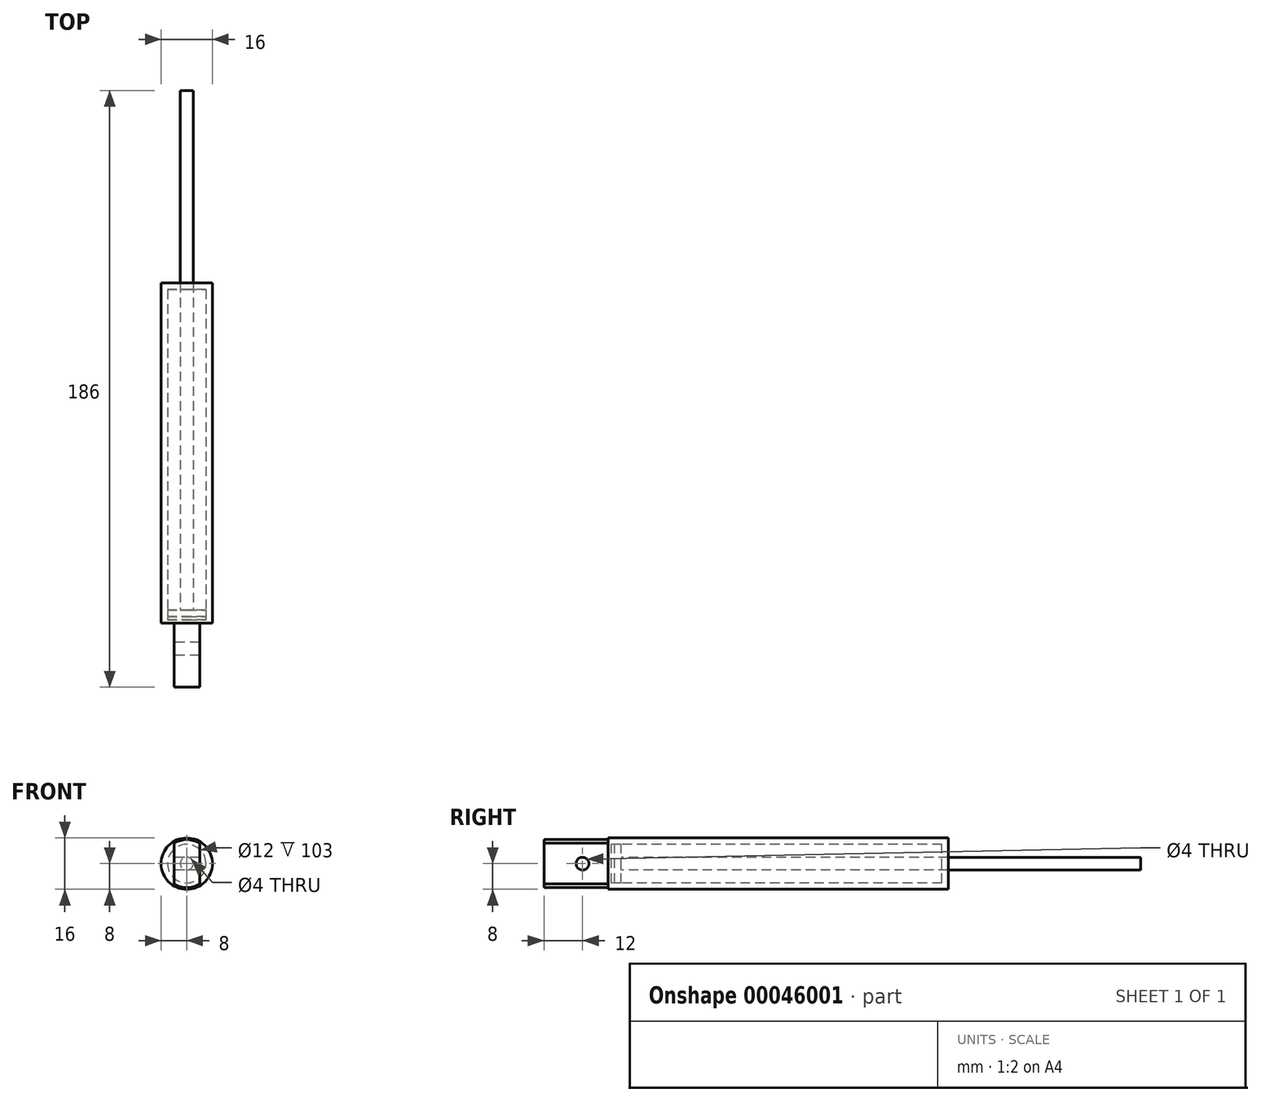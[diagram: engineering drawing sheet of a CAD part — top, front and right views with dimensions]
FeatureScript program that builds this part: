
annotation { "Feature Type Name" : "Feature", "Feature Type Description" : "" }
export const myFeature = defineFeature(function(context is Context, id is Id, definition is map)
    precondition{}
    {
        {
            var Q0;
            Q0=qCreatedBy(makeId("Right.planeOp"),FACE);
            var sketch = newSketch(context, id + "F0", { "sketchPlane" : qUnion([Q0])});
            skLineSegment(sketch, "E0", {"start": v(-96, 0) * mm, "end": v(96, 0) * mm});
            skLineSegment(sketch, "E1", {"start": v(-76, 7.5) * mm, "end": v(-76, 8) * mm});
            skLineSegment(sketch, "E2", {"start": v(-76, 8) * mm, "end": v(30, 8) * mm});
            skLineSegment(sketch, "E3", {"start": v(30, 8) * mm, "end": v(30, 2) * mm});
            skPoint(sketch, "E4.visualSharp", {"position": v(-76, 0) * mm});
            skLineSegment(sketch, "E5", {"start": v(-72, 2) * mm, "end": v(90, 2) * mm});
            skLineSegment(sketch, "E6", {"start": v(-76, 7.5) * mm, "end": v(-96, 7.5) * mm});
            skLineSegment(sketch, "E7", {"start": v(-96, 7.5) * mm, "end": v(-96, 0) * mm});
            skCircle(sketch, "E8", {"center": v(-84, 0) * mm, "radius": 2 * mm});
            skLineSegment(sketch, "E9", {"start": v(90, 2) * mm, "end": v(90, 0) * mm});
            skLineSegment(sketch, "E10", {"start": v(30, 2) * mm, "end": v(28, 2) * mm});
            skLineSegment(sketch, "E11", {"start": v(28, 2) * mm, "end": v(28, 6) * mm});
            skLineSegment(sketch, "E12", {"start": v(28, 6) * mm, "end": v(-75, 6) * mm});
            skLineSegment(sketch, "E13", {"start": v(-75, 6) * mm, "end": v(-75, 0) * mm});
            skLineSegment(sketch, "E14", {"start": v(-72, 2) * mm, "end": v(-72, 6) * mm});
            skLineSegment(sketch, "E15", {"start": v(-72, 6) * mm, "end": v(-74, 6) * mm});
            skLineSegment(sketch, "E16", {"start": v(-74, 6) * mm, "end": v(-74, 0) * mm});
            skSolve(sketch);
        }
        {
            var Q0;
            Q0=makeQuery(id+"F0.imprint","IMPRINT",FACE,{"disambiguationData":[TD([[makeQuery(id+"F0.imprint","IMPRINT",EDGE,{"derivedFrom":sQuery(id+"F0.wireOp",EDGE,"E1")}),-1.0]])]});
            var Q1;
            {var subQ0=sQuery(id+"F0.wireOp",EDGE,"E8");var subQ1=sQuery(id+"F0.wireOp",EDGE,"E0");var subQ3=makeQuery(id+"F0.imprint","INTERSECT",VERTEX,{"disambiguationData":[OD(0.0)],"derivedFrom":[subQ1,subQ0]});Q1=makeQuery(id+"F0.imprint","IMPRINT",FACE,{"disambiguationData":[TD([[makeQuery(id+"F0.imprint","IMPRINT",EDGE,{"disambiguationData":[TD([[subQ3,-1.0]])],"derivedFrom":subQ1}),1.0]])]});}
            var Q2;
            Q2=sQuery(id+"F0.wireOp",EDGE,"E0");
            revolve(context, id + "F1", {"entities" : qUnion([Q0, Q1]), "axis" : qUnion([Q2]), "revolveType" : RevolveType.FULL});
        }
        {
            var Q0;
            {var subQ0=sQuery(id+"F0.wireOp",EDGE,"E9");Q0=makeQuery(id+"F0.imprint","IMPRINT",FACE,{"disambiguationData":[TD([[makeQuery(id+"F0.imprint","IMPRINT",EDGE,{"derivedFrom":subQ0}),-1.0]])]});}
            var Q1;
            Q1=sQuery(id+"F0.wireOp",EDGE,"E0");
            revolve(context, id + "F2", {"entities" : qUnion([Q0]), "axis" : qUnion([Q1]), "revolveType" : RevolveType.FULL});
        }
        {
            var Q0;
            {var subQ0=sQuery(id+"F0.wireOp",EDGE,"E8");var subQ1=sQuery(id+"F0.wireOp",EDGE,"E0");var subQ3=makeQuery(id+"F0.imprint","INTERSECT",VERTEX,{"disambiguationData":[OD(0.0)],"derivedFrom":[subQ1,subQ0]});Q0=makeQuery(id+"F0.imprint","IMPRINT",FACE,{"disambiguationData":[TD([[makeQuery(id+"F0.imprint","IMPRINT",EDGE,{"disambiguationData":[TD([[subQ3,-1.0]])],"derivedFrom":subQ1}),1.0]])]});}
            var Q1;
            {var subQ0=sQuery(id+"F0.wireOp",EDGE,"E8");var subQ1=sQuery(id+"F0.wireOp",EDGE,"E0");var subQ3=makeQuery(id+"F0.imprint","INTERSECT",VERTEX,{"disambiguationData":[OD(0.0)],"derivedFrom":[subQ1,subQ0]});Q1=makeQuery(id+"F0.imprint","IMPRINT",FACE,{"disambiguationData":[TD([[makeQuery(id+"F0.imprint","IMPRINT",EDGE,{"disambiguationData":[TD([[subQ3,-1.0]])],"derivedFrom":subQ1}),-1.0]])]});}
            extrude(context, id + "F3", {"entities" : qUnion([Q0, Q1]), "operationType" : NewBodyOperationType.REMOVE, "endBound" : BoundingType.THROUGH_ALL, "depth" : 25 * mm});
        }
        {
            var Q0;
            {var subQ0=sQuery(id+"F0.wireOp",EDGE,"E8");var subQ1=sQuery(id+"F0.wireOp",EDGE,"E0");var subQ3=makeQuery(id+"F0.imprint","INTERSECT",VERTEX,{"disambiguationData":[OD(0.0)],"derivedFrom":[subQ1,subQ0]});Q0=makeQuery(id+"F0.imprint","IMPRINT",FACE,{"disambiguationData":[TD([[makeQuery(id+"F0.imprint","IMPRINT",EDGE,{"disambiguationData":[TD([[subQ3,-1.0]])],"derivedFrom":subQ1}),-1.0]])]});}
            var Q1;
            {var subQ0=sQuery(id+"F0.wireOp",EDGE,"E8");var subQ1=sQuery(id+"F0.wireOp",EDGE,"E0");var subQ3=makeQuery(id+"F0.imprint","INTERSECT",VERTEX,{"disambiguationData":[OD(0.0)],"derivedFrom":[subQ1,subQ0]});Q1=makeQuery(id+"F0.imprint","IMPRINT",FACE,{"disambiguationData":[TD([[makeQuery(id+"F0.imprint","IMPRINT",EDGE,{"disambiguationData":[TD([[subQ3,-1.0]])],"derivedFrom":subQ1}),1.0]])]});}
            extrude(context, id + "F4", {"entities" : qUnion([Q0, Q1]), "operationType" : NewBodyOperationType.REMOVE, "oppositeDirection" : true, "depth" : 25 * mm});
        }
        {
            var Q0;
            Q0=makeQuery(id+"F1.opRevolve","SWEPT_FACE",FACE,{"disambiguationData":[OSD([sQuery(id+"F0.wireOp",EDGE,"E7")])]});
            var sketch = newSketch(context, id + "F5", { "sketchPlane" : qUnion([Q0])});
            skLineSegment(sketch, "E17.rect.bottom", {"start": v(4, 7.5) * mm, "end": v(-4, 7.5) * mm});
            skLineSegment(sketch, "E17.rect.top", {"start": v(4, -7.5) * mm, "end": v(-4, -7.5) * mm});
            skLineSegment(sketch, "E17.rect.left", {"start": v(4, 7.5) * mm, "end": v(4, -7.5) * mm});
            skLineSegment(sketch, "E17.rect.right", {"start": v(-4, 7.5) * mm, "end": v(-4, -7.5) * mm});
            skPoint(sketch, "E17.rect.middle", {"position": v(0, 0) * mm});
            skLineSegment(sketch, "E18.rect.bottom", {"start": v(7.5, 7.5) * mm, "end": v(-7.5, 7.5) * mm});
            skLineSegment(sketch, "E18.rect.top", {"start": v(7.5, -7.5) * mm, "end": v(-7.5, -7.5) * mm});
            skLineSegment(sketch, "E18.rect.left", {"start": v(7.5, 7.5) * mm, "end": v(7.5, -7.5) * mm});
            skLineSegment(sketch, "E18.rect.right", {"start": v(-7.5, 7.5) * mm, "end": v(-7.5, -7.5) * mm});
            skSolve(sketch);
        }
        {
            var Q0;
            {var subQ0=makeQuery(id+"F1.opRevolve","SWEPT_EDGE",EDGE,{"disambiguationData":[OSD([sQuery(id+"F0.wireOp",EDGE,"E6"),sQuery(id+"F0.wireOp",EDGE,"E7")])]});var subQ1=sQuery(id+"F5.wireOp",EDGE,"E17.rect.right");var subQ3=makeQuery(id+"F5.imprint","INTERSECT",VERTEX,{"disambiguationData":[OD(0.0)],"derivedFrom":[subQ0,subQ1]});Q0=makeQuery(id+"F5.imprint","IMPRINT",FACE,{"disambiguationData":[TD([[makeQuery(id+"F5.imprint","IMPRINT",EDGE,{"disambiguationData":[TD([[subQ3,-1.0]])],"derivedFrom":subQ1}),-1.0]])]});}
            var Q1;
            {var subQ0=makeQuery(id+"F1.opRevolve","SWEPT_EDGE",EDGE,{"disambiguationData":[OSD([sQuery(id+"F0.wireOp",EDGE,"E6"),sQuery(id+"F0.wireOp",EDGE,"E7")])]});var subQ1=sQuery(id+"F5.wireOp",EDGE,"E17.rect.left");var subQ3=makeQuery(id+"F5.imprint","INTERSECT",VERTEX,{"disambiguationData":[OD(0.0)],"derivedFrom":[subQ0,subQ1]});Q1=makeQuery(id+"F5.imprint","IMPRINT",FACE,{"disambiguationData":[TD([[makeQuery(id+"F5.imprint","IMPRINT",EDGE,{"disambiguationData":[TD([[subQ3,-1.0]])],"derivedFrom":subQ1}),1.0]])]});}
            extrude(context, id + "F6", {"entities" : qUnion([Q0, Q1]), "operationType" : NewBodyOperationType.REMOVE, "oppositeDirection" : true, "depth" : 20 * mm});
        }
    });
